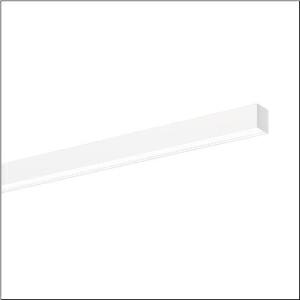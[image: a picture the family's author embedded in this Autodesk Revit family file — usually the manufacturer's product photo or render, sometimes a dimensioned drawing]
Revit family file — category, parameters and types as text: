
# Revit family: silica_r__21_51mx20dc35wb_3ec9
name_source: partatom
category: Lighting Fixtures
units: mm (PartAtom-declared; Revit-internal decimal feet)

## family parameters
Cut with Voids When Loaded = No
Host = Face
Light Source = No
Part Type = Normal
Room Calculation Point = No
Round Connector Dimension = Use Diameter
Shared = No

## types (1)
- --- (1 x LED, 6000 lm, 42.6 W, 3000K)
    Apparent Load = 43 VA
    CIE Flux Codes = 48 79 96 100 100
    Color Rendering = 80
    Color Temperature = 3000K
    Default Elevation = 1800 mm
    Description = Silica® 21, office luminaire, primary optical cover: cover, of PMMA, opal, light emission: direct distribution, primary light characteristic: symmetric, installation type: surface-mounted, LED, rated luminous flux: 6.000lm, luminous efficacy: 141lm/W, light colour: 830, colour temperature: 3000K, with terminal, 3+2-pole, max. 2.5mm², mains connection: 220..240V, AC, 50/60Hz, rated input power: 42.6W, luminaire housing, of aluminium, traffic white (RAL 9016), length: 3.004mm, width: 53mm, height: 53mm, protection rating (complete): IP20, insulation class (complete): insulation class I (protective earthing), certification: CE, permissible operating ambient temperature: 0..+35°C, standard: EN 50419, packaging unit: 1 piece
    Height = 0 mm  [stored 0 ft]
    Lamp = 1 x LED
    Lamp Light Flux = 6000 lm
    Lamp Power = 42.6 W
    Lamp count = 1
    Length = 3004 mm
    Luminous efficacy = 141 lm/W
    Manufacturer = Siteco
    ModVariant = No
    Model = 51MX20DC35WB
    Mounting Place = Ceiling
    Mounting Type = Recessed
    Number of Poles = 1
    OnlyDefault = Yes
    Power Factor = 1
    Product Name = Silica® 21
    Product group = office luminaire | ceiling recessed
    ProductGroupID = 400
    Protection Class = Protection class I
    Protection Degree = IP 20
    RLX_Detail_Level = 1
    RLX_Emergency_Light_Flux = 0 lm
    RLX_Emergency_Type = 0
    RLX_Emergency_Type_DB = No
    RlxData = <blob elided: 23957 chars, md5=3f3f86f2>
    Socket = socket
    Standby Power = 0 W
    System Light Flux = 6000 lm
    System Power = 43 W
    Type Comments = factory setting: luminous flux: 100 % | dim-lin: 254 | 233 mA
    Type Image = l_1335877.jpg
    URL = http://relux.com
    VarID = @adj_086855
    Voltage = 0 V
    Weight = 0.00 kg
    Width = 53 mm

note: [stored X ft] marks values corroborated as IEEE doubles in the binary element streams (Revit-internal decimal feet)

## geometry (parser evidence)
native form markers: Blend x4, Sweep x9
no freeform markers — native parametric forms only
